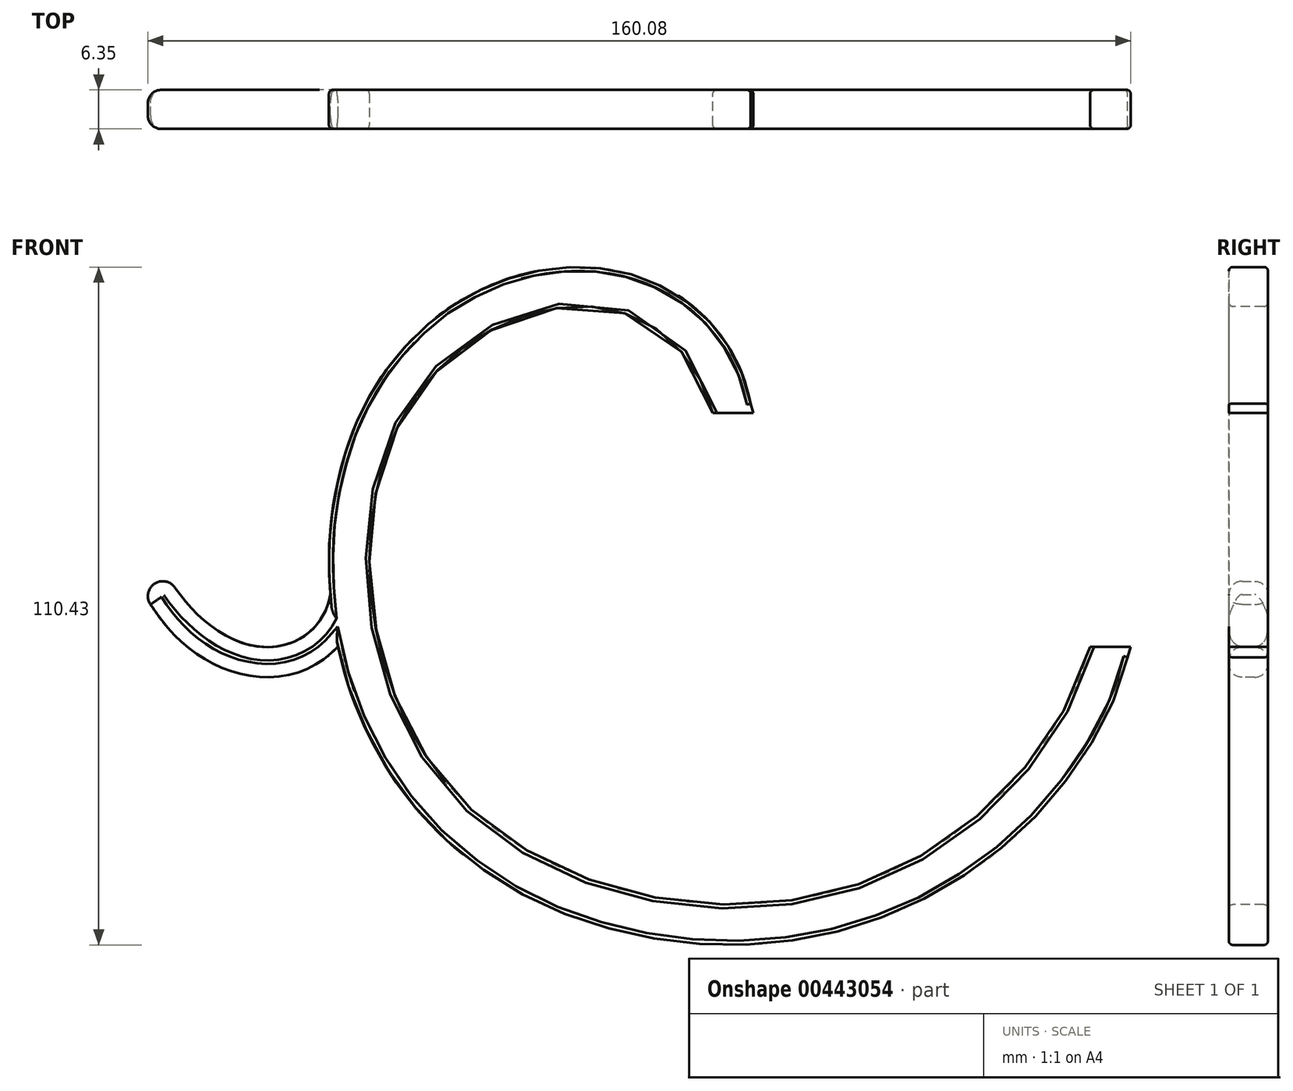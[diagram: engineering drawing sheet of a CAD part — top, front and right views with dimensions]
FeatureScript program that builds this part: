
annotation { "Feature Type Name" : "Feature", "Feature Type Description" : "" }
export const myFeature = defineFeature(function(context is Context, id is Id, definition is map)
    precondition{}
    {
        {
            var Q0;
            Q0=qCreatedBy(makeId("Front.planeOp"),FACE);
            var sketch = newSketch(context, id + "F0", { "sketchPlane" : qUnion([Q0])});
            skLineSegment(sketch, "E0.bottom", {"start": v(0, 0) * mm, "end": v(127, 0) * mm, "construction": true});
            skLineSegment(sketch, "E0.top", {"start": v(0, 38.1) * mm, "end": v(127, 38.1) * mm, "construction": true});
            skLineSegment(sketch, "E0.left", {"start": v(0, 0) * mm, "end": v(0, 38.1) * mm, "construction": true});
            skLineSegment(sketch, "E0.right", {"start": v(127, 0) * mm, "end": v(127, 38.1) * mm, "construction": true});
            skFitSpline(sketch, "E1", {"points": [v(25.4, 38.1) * mm, v(8.02, 55.13) * mm, v(-24.7, 38.16) * mm, v(-17.84, -22.46) * mm, v(48.03, -39.02) * mm, v(86.82, 0) * mm], "startDerivative": vector(-44.59, 179.63) * mm, "endDerivative": vector(59.95, 217.95) * mm});
            skFitSpline(sketch, "E2.0", {"points": [v(31.56, 39.63) * mm, v(30.98, 41.97) * mm, v(29.3, 46.46) * mm, v(25.34, 52.4) * mm, v(20.92, 56.42) * mm, v(16.77, 58.9) * mm, v(13.94, 60.12) * mm, v(11.57, 60.86) * mm, v(9.73, 61.3) * mm, v(7.85, 61.6) * mm, v(5.31, 61.85) * mm, v(2.1, 61.85) * mm, v(-3.07, 61.26) * mm, v(-9.5, 59.44) * mm, v(-16.9, 55.64) * mm, v(-22.54, 51.15) * mm, v(-26.54, 46.77) * mm, v(-28.77, 43.72) * mm, v(-30.38, 41.08) * mm, v(-31.84, 38.34) * mm, v(-33.4, 34.75) * mm, v(-34.87, 30.22) * mm, v(-36.3, 23.96) * mm, v(-37.11, 15.79) * mm, v(-36.6, 5.74) * mm, v(-34.58, -4.28) * mm, v(-31.63, -12.33) * mm, v(-28.47, -18.44) * mm, v(-26.16, -22.08) * mm, v(-24.1, -24.85) * mm, v(-22.45, -26.87) * mm, v(-20.7, -28.79) * mm, v(-18.26, -31.23) * mm, v(-15, -34.05) * mm, v(-9.4, -38.07) * mm, v(-1.8, -42.2) * mm, v(8, -45.71) * mm, v(18.23, -47.83) * mm, v(28.63, -48.54) * mm, v(37.23, -47.95) * mm, v(43.96, -46.75) * mm, v(48.07, -45.7) * mm, v(51.28, -44.65) * mm, v(54.43, -43.49) * mm, v(58.24, -41.82) * mm, v(62.58, -39.51) * mm, v(68.06, -36.06) * mm, v(74.32, -31.11) * mm, v(80.78, -24.41) * mm, v(86.14, -17.16) * mm, v(90.3, -9.53) * mm, v(92.22, -4.3) * mm, v(92.94, -1.68) * mm]});
            skLineSegment(sketch, "E3", {"start": v(31.56, 39.63) * mm, "end": v(31.98, 38.1) * mm});
            skLineSegment(sketch, "E4", {"start": v(31.98, 38.1) * mm, "end": v(25.4, 38.1) * mm});
            skLineSegment(sketch, "E5", {"start": v(92.94, -1.68) * mm, "end": v(93.45, 0) * mm});
            skLineSegment(sketch, "E6", {"start": v(93.45, 0) * mm, "end": v(86.82, 0) * mm});
            skFitSpline(sketch, "E7", {"points": [v(-36.73, 9.72) * mm, v(-46.32, 0) * mm, v(-62.23, 9.66) * mm], "startDerivative": vector(-3.53, -39.21) * mm, "endDerivative": vector(-24.57, 35.7) * mm});
            skFitSpline(sketch, "E8.0", {"points": [v(-31.92, 9.29) * mm, v(-32.02, 8.18) * mm, v(-32.42, 6.05) * mm, v(-33.57, 3.14) * mm, v(-35.22, 0.62) * mm, v(-37.28, -1.46) * mm, v(-39.64, -3.05) * mm, v(-42.21, -4.16) * mm, v(-44.9, -4.78) * mm, v(-47.66, -4.93) * mm, v(-50.37, -4.62) * mm, v(-53.88, -3.67) * mm, v(-58, -1.58) * mm, v(-62.44, 2.08) * mm, v(-65.02, 5.2) * mm, v(-66.2, 6.92) * mm]});
            skCircle(sketch, "E9", {"center": v(-64.21, 8.3) * mm, "radius": 2.41 * mm});
            skPoint(sketch, "E9.third.point", {"position": v(-66.2, 9.66) * mm});
            skSolve(sketch);
        }
        {
            var Q0;
            Q0 = qSketchRegion(id + "F0", true);
            extrude(context, id + "F1", {"entities" : qUnion([Q0]), "depth" : 6.35 * mm});
        }
        {
            var Q0;
            Q0=makeQuery(id+"F1.opExtrude","CAP_EDGE",EDGE,{"disambiguationData":[OSD([sQuery(id+"F0.wireOp",EDGE,"E1")])],"isStart":false});
            var Q1;
            {var subQ0=sQuery(id+"F0.wireOp",EDGE,"E2.0");Q1=makeQuery(id+"F1.opExtrude","CAP_EDGE",EDGE,{"disambiguationData":[OSD([subQ0]),TDD([makeQuery(id+"F0.imprint","IMPRINT",EDGE,{"disambiguationData":[TD([[makeQuery(id+"F0.imprint","INTERSECT",VERTEX,{"derivedFrom":[subQ0,sQuery(id+"F0.wireOp",EDGE,"E3")]}),-1.0]])],"derivedFrom":subQ0})])],"isStart":true});}
            var Q2;
            {var subQ0=sQuery(id+"F0.wireOp",EDGE,"E2.0");Q2=makeQuery(id+"F1.opExtrude","CAP_EDGE",EDGE,{"disambiguationData":[OSD([subQ0]),TDD([makeQuery(id+"F0.imprint","IMPRINT",EDGE,{"disambiguationData":[TD([[makeQuery(id+"F0.imprint","INTERSECT",VERTEX,{"derivedFrom":[subQ0,sQuery(id+"F0.wireOp",EDGE,"E3")]}),-1.0]])],"derivedFrom":subQ0})])],"isStart":false});}
            var Q3;
            {var subQ0=sQuery(id+"F0.wireOp",EDGE,"E2.0");Q3=makeQuery(id+"F1.opExtrude","CAP_EDGE",EDGE,{"disambiguationData":[OSD([subQ0]),TDD([makeQuery(id+"F0.imprint","IMPRINT",EDGE,{"disambiguationData":[TD([[makeQuery(id+"F0.imprint","INTERSECT",VERTEX,{"derivedFrom":[subQ0,sQuery(id+"F0.wireOp",EDGE,"E5")]}),1.0]])],"derivedFrom":subQ0})])],"isStart":false});}
            var Q4;
            {var subQ0=sQuery(id+"F0.wireOp",EDGE,"E2.0");Q4=makeQuery(id+"F1.opExtrude","CAP_EDGE",EDGE,{"disambiguationData":[OSD([subQ0]),TDD([makeQuery(id+"F0.imprint","IMPRINT",EDGE,{"disambiguationData":[TD([[makeQuery(id+"F0.imprint","INTERSECT",VERTEX,{"derivedFrom":[subQ0,sQuery(id+"F0.wireOp",EDGE,"E5")]}),1.0]])],"derivedFrom":subQ0})])],"isStart":true});}
            var Q5;
            Q5=makeQuery(id+"F1.opExtrude","CAP_EDGE",EDGE,{"disambiguationData":[OSD([sQuery(id+"F0.wireOp",EDGE,"E1")])],"isStart":true});
            fillet(context, id + "F2", {"entities" : qUnion([Q0, Q1, Q2, Q3, Q4, Q5]), "radius" : 0.64 * mm, "tangentPropagation" : true, "allowEdgeOverflow" : false});
        }
        {
            var Q0;
            Q0=makeQuery(id+"F1.opExtrude","CAP_EDGE",EDGE,{"disambiguationData":[OSD([sQuery(id+"F0.wireOp",EDGE,"E7")])],"isStart":false});
            var Q1;
            Q1=makeQuery(id+"F1.opExtrude","CAP_EDGE",EDGE,{"disambiguationData":[OSD([sQuery(id+"F0.wireOp",EDGE,"E8.0")])],"isStart":false});
            var Q2;
            Q2=makeQuery(id+"F1.opExtrude","CAP_EDGE",EDGE,{"disambiguationData":[OSD([sQuery(id+"F0.wireOp",EDGE,"E8.0")])],"isStart":true});
            var Q3;
            Q3=makeQuery(id+"F1.opExtrude","CAP_EDGE",EDGE,{"disambiguationData":[OSD([sQuery(id+"F0.wireOp",EDGE,"E7")])],"isStart":true});
            fillet(context, id + "F3", {"entities" : qUnion([Q0, Q1, Q2, Q3]), "radius" : 2.16 * mm, "tangentPropagation" : true, "allowEdgeOverflow" : false});
        }
    });
